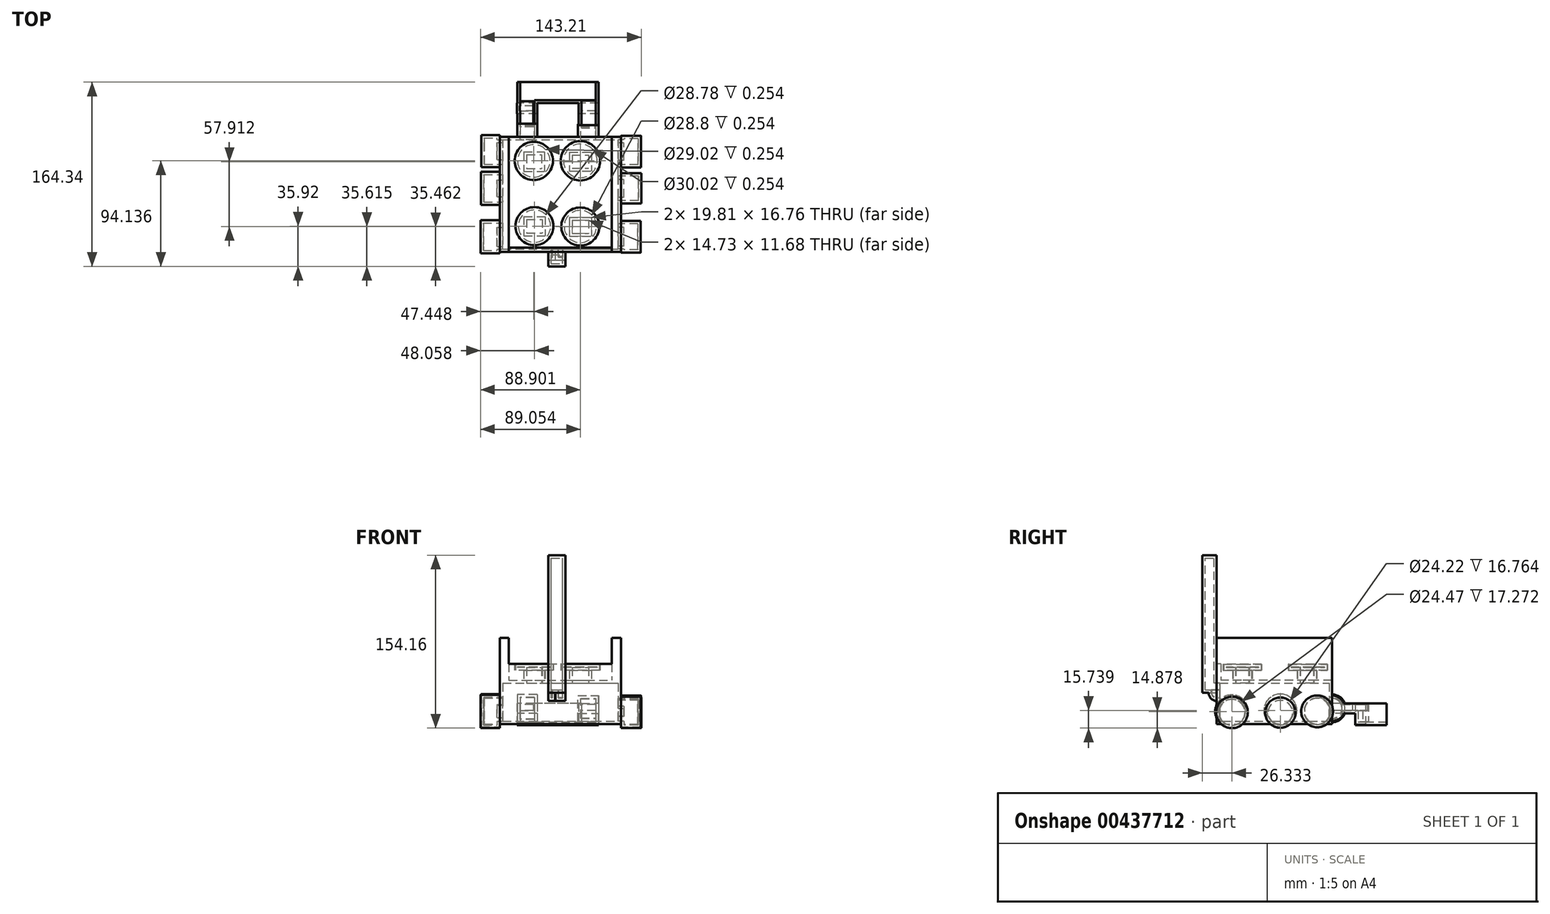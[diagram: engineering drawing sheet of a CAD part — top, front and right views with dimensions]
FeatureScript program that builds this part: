
annotation { "Feature Type Name" : "Feature", "Feature Type Description" : "" }
export const myFeature = defineFeature(function(context is Context, id is Id, definition is map)
    precondition{}
    {
        {
            var Q0;
            Q0=qCreatedBy(makeId("Front.planeOp"),FACE);
            var sketch = newSketch(context, id + "F0", { "sketchPlane" : qUnion([Q0])});
            skLineSegment(sketch, "E0.bottom", {"start": v(-50.6, 20.57) * mm, "end": v(57.3, 20.57) * mm});
            skLineSegment(sketch, "E0.top", {"start": v(-50.6, -18.44) * mm, "end": v(57.3, -18.44) * mm});
            skLineSegment(sketch, "E0.left", {"start": v(-50.6, 20.57) * mm, "end": v(-50.6, -18.44) * mm});
            skLineSegment(sketch, "E0.right", {"start": v(57.3, 20.57) * mm, "end": v(57.3, -18.44) * mm});
            skSolve(sketch);
        }
        {
            var Q0;
            Q0 = qSketchRegion(id + "F0", true);
            extrude(context, id + "F1", {"entities" : qUnion([Q0]), "depth" : 56.64 * mm});
        }
        {
            var Q0;
            Q0=makeQuery(id+"F1.opExtrude","CAP_FACE",FACE,{"disambiguationData":[OSD([sQuery(id+"F0.wireOp",EDGE,"E0.bottom"),sQuery(id+"F0.wireOp",EDGE,"E0.top"),sQuery(id+"F0.wireOp",EDGE,"E0.left"),sQuery(id+"F0.wireOp",EDGE,"E0.right")])],"isStart":true});
            extrude(context, id + "F2", {"entities" : qUnion([Q0]), "operationType" : NewBodyOperationType.ADD, "depth" : 45.97 * mm});
        }
        {
            var Q0;
            {var subQ0=sQuery(id+"F0.wireOp",EDGE,"E0.right");Q0=makeQuery(id+"F2.boolean.opBoolean","MERGE",FACE,{"derivedFrom":[makeQuery(id+"F1.opExtrude","SWEPT_FACE",FACE,{"disambiguationData":[OSD([subQ0])]}),makeQuery(id+"F2.opExtrude","SWEPT_FACE",FACE,{"disambiguationData":[OSD([subQ0])]})]});}
            var sketch = newSketch(context, id + "F3", { "sketchPlane" : qUnion([Q0])});
            skCircle(sketch, "E1", {"center": v(-43.07, -8.03) * mm, "radius": 14.07 * mm});
            skSolve(sketch);
        }
        {
            var Q0;
            Q0 = qSketchRegion(id + "F3", true);
            extrude(context, id + "F4", {"entities" : qUnion([Q0]), "operationType" : NewBodyOperationType.ADD, "depth" : 17.53 * mm});
        }
        {
            var Q0;
            {var subQ0=sQuery(id+"F0.wireOp",EDGE,"E0.bottom");var subQ1=sQuery(id+"F0.wireOp",EDGE,"E0.top");var subQ2=sQuery(id+"F0.wireOp",EDGE,"E0.right");var subQ3=sQuery(id+"F0.wireOp",EDGE,"E0.left");var subQ4=sQuery(id+"F3.wireOp",EDGE,"E1");Q0=makeQuery(id+"F4.boolean.opBoolean","SPLIT",FACE,{"disambiguationData":[TD([makeQuery(id+"F1.opExtrude","SWEPT_FACE",FACE,{"disambiguationData":[OSD([subQ0])]}),makeQuery(id+"F1.opExtrude","CAP_FACE",FACE,{"disambiguationData":[OSD([subQ0,subQ1,subQ3,subQ2])],"isStart":false}),makeQuery(id+"F1.opExtrude","SWEPT_FACE",FACE,{"disambiguationData":[OSD([subQ1])]}),makeQuery(id+"F2.opExtrude","SWEPT_FACE",FACE,{"disambiguationData":[OSD([subQ0])]}),makeQuery(id+"F2.opExtrude","SWEPT_FACE",FACE,{"disambiguationData":[OSD([subQ1])]}),makeQuery(id+"F2.opExtrude","CAP_FACE",FACE,{"disambiguationData":[OSD([subQ0,subQ1,subQ3,subQ2])],"isStart":false}),makeQuery(id+"F4.opExtrude","SWEPT_FACE",FACE,{"disambiguationData":[OSD([subQ4])]}),makeQuery(id+"F4.opExtrude","CAP_FACE",FACE,{"disambiguationData":[OSD([subQ4])],"isStart":true})])],"derivedFrom":makeQuery(id+"F2.boolean.opBoolean","MERGE",FACE,{"derivedFrom":[makeQuery(id+"F1.opExtrude","SWEPT_FACE",FACE,{"disambiguationData":[OSD([subQ2])]}),makeQuery(id+"F2.opExtrude","SWEPT_FACE",FACE,{"disambiguationData":[OSD([subQ2])]})]})});}
            var sketch = newSketch(context, id + "F5", { "sketchPlane" : qUnion([Q0])});
            skCircle(sketch, "E2", {"center": v(0, -8.32) * mm, "radius": 13.5 * mm});
            skSolve(sketch);
        }
        {
            var Q0;
            Q0 = qSketchRegion(id + "F5", true);
            extrude(context, id + "F6", {"entities" : qUnion([Q0]), "operationType" : NewBodyOperationType.ADD, "depth" : 18.03 * mm});
        }
        {
            var Q0;
            {var subQ0=sQuery(id+"F0.wireOp",EDGE,"E0.bottom");var subQ1=sQuery(id+"F0.wireOp",EDGE,"E0.top");var subQ2=sQuery(id+"F0.wireOp",EDGE,"E0.right");var subQ3=sQuery(id+"F0.wireOp",EDGE,"E0.left");var subQ4=sQuery(id+"F3.wireOp",EDGE,"E1");Q0=makeQuery(id+"F4.boolean.opBoolean","SPLIT",FACE,{"disambiguationData":[TD([makeQuery(id+"F1.opExtrude","SWEPT_FACE",FACE,{"disambiguationData":[OSD([subQ0])]}),makeQuery(id+"F1.opExtrude","CAP_FACE",FACE,{"disambiguationData":[OSD([subQ0,subQ1,subQ3,subQ2])],"isStart":false}),makeQuery(id+"F1.opExtrude","SWEPT_FACE",FACE,{"disambiguationData":[OSD([subQ1])]}),makeQuery(id+"F2.opExtrude","SWEPT_FACE",FACE,{"disambiguationData":[OSD([subQ0])]}),makeQuery(id+"F2.opExtrude","SWEPT_FACE",FACE,{"disambiguationData":[OSD([subQ1])]}),makeQuery(id+"F2.opExtrude","CAP_FACE",FACE,{"disambiguationData":[OSD([subQ0,subQ1,subQ3,subQ2])],"isStart":false}),makeQuery(id+"F4.opExtrude","SWEPT_FACE",FACE,{"disambiguationData":[OSD([subQ4])]}),makeQuery(id+"F4.opExtrude","CAP_FACE",FACE,{"disambiguationData":[OSD([subQ4])],"isStart":true})])],"derivedFrom":makeQuery(id+"F2.boolean.opBoolean","MERGE",FACE,{"derivedFrom":[makeQuery(id+"F1.opExtrude","SWEPT_FACE",FACE,{"disambiguationData":[OSD([subQ2])]}),makeQuery(id+"F2.opExtrude","SWEPT_FACE",FACE,{"disambiguationData":[OSD([subQ2])]})]})});}
            var sketch = newSketch(context, id + "F7", { "sketchPlane" : qUnion([Q0])});
            skCircle(sketch, "E3", {"center": v(32.74, -7.15) * mm, "radius": 14.18 * mm});
            skSolve(sketch);
        }
        {
            var Q0;
            Q0 = qSketchRegion(id + "F7", true);
            extrude(context, id + "F8", {"entities" : qUnion([Q0]), "operationType" : NewBodyOperationType.ADD, "depth" : 17.78 * mm});
        }
        {
            var Q0;
            {var subQ0=sQuery(id+"F0.wireOp",EDGE,"E0.left");Q0=makeQuery(id+"F2.boolean.opBoolean","MERGE",FACE,{"derivedFrom":[makeQuery(id+"F1.opExtrude","SWEPT_FACE",FACE,{"disambiguationData":[OSD([subQ0])]}),makeQuery(id+"F2.opExtrude","SWEPT_FACE",FACE,{"disambiguationData":[OSD([subQ0])]})]});}
            var sketch = newSketch(context, id + "F9", { "sketchPlane" : qUnion([Q0])});
            skCircle(sketch, "E4", {"center": v(-33.23, -6.92) * mm, "radius": 14.3 * mm});
            skSolve(sketch);
        }
        {
            var Q0;
            Q0 = qSketchRegion(id + "F9", true);
            extrude(context, id + "F10", {"entities" : qUnion([Q0]), "operationType" : NewBodyOperationType.ADD, "depth" : 16.5 * mm});
        }
        {
            var Q0;
            {var subQ0=sQuery(id+"F0.wireOp",EDGE,"E0.bottom");var subQ1=sQuery(id+"F9.wireOp",EDGE,"E4");var subQ2=sQuery(id+"F0.wireOp",EDGE,"E0.top");var subQ3=sQuery(id+"F0.wireOp",EDGE,"E0.right");var subQ4=sQuery(id+"F0.wireOp",EDGE,"E0.left");Q0=makeQuery(id+"F10.boolean.opBoolean","SPLIT",FACE,{"disambiguationData":[TD([makeQuery(id+"F1.opExtrude","SWEPT_FACE",FACE,{"disambiguationData":[OSD([subQ0])]}),makeQuery(id+"F1.opExtrude","CAP_FACE",FACE,{"disambiguationData":[OSD([subQ0,subQ2,subQ4,subQ3])],"isStart":false}),makeQuery(id+"F1.opExtrude","SWEPT_FACE",FACE,{"disambiguationData":[OSD([subQ2])]}),makeQuery(id+"F2.opExtrude","SWEPT_FACE",FACE,{"disambiguationData":[OSD([subQ0])]}),makeQuery(id+"F2.opExtrude","SWEPT_FACE",FACE,{"disambiguationData":[OSD([subQ2])]}),makeQuery(id+"F2.opExtrude","CAP_FACE",FACE,{"disambiguationData":[OSD([subQ0,subQ2,subQ4,subQ3])],"isStart":false}),makeQuery(id+"F10.opExtrude","SWEPT_FACE",FACE,{"disambiguationData":[OSD([subQ1])]}),makeQuery(id+"F10.opExtrude","CAP_FACE",FACE,{"disambiguationData":[OSD([subQ1])],"isStart":true})])],"derivedFrom":makeQuery(id+"F2.boolean.opBoolean","MERGE",FACE,{"derivedFrom":[makeQuery(id+"F1.opExtrude","SWEPT_FACE",FACE,{"disambiguationData":[OSD([subQ4])]}),makeQuery(id+"F2.opExtrude","SWEPT_FACE",FACE,{"disambiguationData":[OSD([subQ4])]})]})});}
            var sketch = newSketch(context, id + "F11", { "sketchPlane" : qUnion([Q0])});
            skCircle(sketch, "E5", {"center": v(0, -6.35) * mm, "radius": 14.65 * mm});
            skSolve(sketch);
        }
        {
            var Q0;
            Q0 = qSketchRegion(id + "F11", true);
            extrude(context, id + "F12", {"entities" : qUnion([Q0]), "operationType" : NewBodyOperationType.ADD, "depth" : 16.76 * mm});
        }
        {
            var Q0;
            {var subQ0=sQuery(id+"F0.wireOp",EDGE,"E0.bottom");var subQ1=sQuery(id+"F9.wireOp",EDGE,"E4");var subQ2=sQuery(id+"F0.wireOp",EDGE,"E0.top");var subQ3=sQuery(id+"F0.wireOp",EDGE,"E0.right");var subQ4=sQuery(id+"F0.wireOp",EDGE,"E0.left");Q0=makeQuery(id+"F10.boolean.opBoolean","SPLIT",FACE,{"disambiguationData":[TD([makeQuery(id+"F1.opExtrude","SWEPT_FACE",FACE,{"disambiguationData":[OSD([subQ0])]}),makeQuery(id+"F1.opExtrude","CAP_FACE",FACE,{"disambiguationData":[OSD([subQ0,subQ2,subQ4,subQ3])],"isStart":false}),makeQuery(id+"F1.opExtrude","SWEPT_FACE",FACE,{"disambiguationData":[OSD([subQ2])]}),makeQuery(id+"F2.opExtrude","SWEPT_FACE",FACE,{"disambiguationData":[OSD([subQ0])]}),makeQuery(id+"F2.opExtrude","SWEPT_FACE",FACE,{"disambiguationData":[OSD([subQ2])]}),makeQuery(id+"F2.opExtrude","CAP_FACE",FACE,{"disambiguationData":[OSD([subQ0,subQ2,subQ4,subQ3])],"isStart":false}),makeQuery(id+"F10.opExtrude","SWEPT_FACE",FACE,{"disambiguationData":[OSD([subQ1])]}),makeQuery(id+"F10.opExtrude","CAP_FACE",FACE,{"disambiguationData":[OSD([subQ1])],"isStart":true})])],"derivedFrom":makeQuery(id+"F2.boolean.opBoolean","MERGE",FACE,{"derivedFrom":[makeQuery(id+"F1.opExtrude","SWEPT_FACE",FACE,{"disambiguationData":[OSD([subQ4])]}),makeQuery(id+"F2.opExtrude","SWEPT_FACE",FACE,{"disambiguationData":[OSD([subQ4])]})]})});}
            var sketch = newSketch(context, id + "F13", { "sketchPlane" : qUnion([Q0])});
            skCircle(sketch, "E6", {"center": v(43.27, -7.21) * mm, "radius": 14.77 * mm});
            skSolve(sketch);
        }
        {
            var Q0;
            Q0 = qSketchRegion(id + "F13", true);
            extrude(context, id + "F14", {"entities" : qUnion([Q0]), "operationType" : NewBodyOperationType.ADD, "depth" : 17.27 * mm});
        }
        {
            var Q0;
            Q0=makeQuery(id+"F2.opExtrude","CAP_FACE",FACE,{"disambiguationData":[OSD([sQuery(id+"F0.wireOp",EDGE,"E0.bottom"),sQuery(id+"F0.wireOp",EDGE,"E0.top"),sQuery(id+"F0.wireOp",EDGE,"E0.left"),sQuery(id+"F0.wireOp",EDGE,"E0.right")])],"isStart":false});
            var sketch = newSketch(context, id + "F15", { "sketchPlane" : qUnion([Q0])});
            skLineSegment(sketch, "E7.bottom", {"start": v(-37.25, 0) * mm, "end": v(-19.46, 0) * mm});
            skLineSegment(sketch, "E7.top", {"start": v(-37.25, -8.93) * mm, "end": v(-19.46, -8.93) * mm});
            skLineSegment(sketch, "E7.left", {"start": v(-37.25, 0) * mm, "end": v(-37.25, -8.93) * mm});
            skLineSegment(sketch, "E7.right", {"start": v(-19.46, 0) * mm, "end": v(-19.46, -8.93) * mm});
            skLineSegment(sketch, "E8.bottom", {"start": v(17.28, 0) * mm, "end": v(35.07, 0) * mm});
            skLineSegment(sketch, "E8.top", {"start": v(17.28, -8.93) * mm, "end": v(35.07, -8.93) * mm});
            skLineSegment(sketch, "E8.left", {"start": v(17.28, 0) * mm, "end": v(17.28, -8.93) * mm});
            skLineSegment(sketch, "E8.right", {"start": v(35.07, 0) * mm, "end": v(35.07, -8.93) * mm});
            skSolve(sketch);
        }
        {
            var Q0;
            Q0 = qSketchRegion(id + "F15", true);
            extrude(context, id + "F16", {"entities" : qUnion([Q0]), "operationType" : NewBodyOperationType.ADD, "depth" : 20.57 * mm});
        }
        {
            var Q0;
            Q0=makeQuery(id+"F16.opExtrude","CAP_FACE",FACE,{"disambiguationData":[OSD([sQuery(id+"F15.wireOp",EDGE,"E7.bottom"),sQuery(id+"F15.wireOp",EDGE,"E7.top"),sQuery(id+"F15.wireOp",EDGE,"E7.left"),sQuery(id+"F15.wireOp",EDGE,"E7.right")])],"isStart":false});
            var sketch = newSketch(context, id + "F17", { "sketchPlane" : qUnion([Q0])});
            skLineSegment(sketch, "E9.bottom", {"start": v(-37.25, 0) * mm, "end": v(-19.46, 0) * mm});
            skLineSegment(sketch, "E9.top", {"start": v(-37.25, -19.27) * mm, "end": v(-19.46, -19.27) * mm});
            skLineSegment(sketch, "E9.left", {"start": v(-37.25, 0) * mm, "end": v(-37.25, -19.27) * mm});
            skLineSegment(sketch, "E9.right", {"start": v(-19.46, 0) * mm, "end": v(-19.46, -19.27) * mm});
            skLineSegment(sketch, "E10.bottom", {"start": v(17.47, 0) * mm, "end": v(35.27, 0) * mm});
            skLineSegment(sketch, "E10.top", {"start": v(17.47, -19.55) * mm, "end": v(35.27, -19.55) * mm});
            skLineSegment(sketch, "E10.left", {"start": v(17.47, 0) * mm, "end": v(17.47, -19.55) * mm});
            skLineSegment(sketch, "E10.right", {"start": v(35.27, 0) * mm, "end": v(35.27, -19.55) * mm});
            skSolve(sketch);
        }
        {
            var Q0;
            Q0 = qSketchRegion(id + "F17", true);
            extrude(context, id + "F18", {"entities" : qUnion([Q0]), "operationType" : NewBodyOperationType.ADD, "depth" : 9.4 * mm});
        }
        {
            var Q0;
            Q0=makeQuery(id+"F1.opExtrude","CAP_FACE",FACE,{"disambiguationData":[OSD([sQuery(id+"F0.wireOp",EDGE,"E0.bottom"),sQuery(id+"F0.wireOp",EDGE,"E0.top"),sQuery(id+"F0.wireOp",EDGE,"E0.left"),sQuery(id+"F0.wireOp",EDGE,"E0.right")])],"isStart":false});
            var sketch = newSketch(context, id + "F19", { "sketchPlane" : qUnion([Q0])});
            skLineSegment(sketch, "E11.bottom", {"start": v(-7.4, 9.33) * mm, "end": v(7.74, 9.33) * mm});
            skLineSegment(sketch, "E11.top", {"start": v(-7.4, 132.07) * mm, "end": v(7.74, 132.07) * mm});
            skLineSegment(sketch, "E11.left", {"start": v(-7.4, 9.33) * mm, "end": v(-7.4, 132.07) * mm});
            skLineSegment(sketch, "E11.right", {"start": v(7.74, 9.33) * mm, "end": v(7.74, 132.07) * mm});
            skSolve(sketch);
        }
        {
            var Q0;
            Q0 = qSketchRegion(id + "F19", true);
            extrude(context, id + "F20", {"entities" : qUnion([Q0]), "operationType" : NewBodyOperationType.ADD, "depth" : 12.95 * mm});
        }
        {
            var Q0;
            Q0=makeQuery(id+"F20.opExtrude","SWEPT_FACE",FACE,{"disambiguationData":[OSD([sQuery(id+"F19.wireOp",EDGE,"E11.left")])]});
            var sketch = newSketch(context, id + "F21", { "sketchPlane" : qUnion([Q0])});
            skCircle(sketch, "E12", {"center": v(55.15, 11.38) * mm, "radius": 9.31 * mm});
            skPoint(sketch, "E12.first.point", {"position": v(63.75, 14.95) * mm});
            skPoint(sketch, "E12.first.point.positionSnap0", {"position": v(56.64, 14.95) * mm});
            skPoint(sketch, "E12.second.point", {"position": v(46.93, 7) * mm});
            skPoint(sketch, "E12.third.point", {"position": v(56.64, 20.57) * mm});
            skSolve(sketch);
        }
        {
            var Q0;
            Q0 = qSketchRegion(id + "F21", true);
            extrude(context, id + "F22", {"entities" : qUnion([Q0]), "operationType" : NewBodyOperationType.ADD, "oppositeDirection" : true, "depth" : 6.1 * mm});
        }
        {
            var Q0;
            Q0=makeQuery(id+"F20.opExtrude","SWEPT_FACE",FACE,{"disambiguationData":[OSD([sQuery(id+"F19.wireOp",EDGE,"E11.right")])]});
            var sketch = newSketch(context, id + "F23", { "sketchPlane" : qUnion([Q0])});
            skCircle(sketch, "E13", {"center": v(-56.64, 9.33) * mm, "radius": 7.21 * mm});
            skSolve(sketch);
        }
        {
            var Q0;
            Q0 = qSketchRegion(id + "F23", true);
            extrude(context, id + "F24", {"entities" : qUnion([Q0]), "operationType" : NewBodyOperationType.ADD, "oppositeDirection" : true, "depth" : 8.9 * mm});
        }
        {
            var Q0;
            {var subQ0=sQuery(id+"F0.wireOp",EDGE,"E0.bottom");Q0=makeQuery(id+"F2.boolean.opBoolean","MERGE",FACE,{"derivedFrom":[makeQuery(id+"F1.opExtrude","SWEPT_FACE",FACE,{"disambiguationData":[OSD([subQ0])]}),makeQuery(id+"F2.opExtrude","SWEPT_FACE",FACE,{"disambiguationData":[OSD([subQ0])]})]});}
            var sketch = newSketch(context, id + "F25", { "sketchPlane" : qUnion([Q0])});
            skLineSegment(sketch, "E14.bottom", {"start": v(-29.26, -25.15) * mm, "end": v(-10.36, -25.15) * mm});
            skLineSegment(sketch, "E14.top", {"start": v(-29.26, -42.21) * mm, "end": v(-10.36, -42.21) * mm});
            skLineSegment(sketch, "E14.left", {"start": v(-29.26, -25.15) * mm, "end": v(-29.26, -42.21) * mm});
            skLineSegment(sketch, "E14.right", {"start": v(-10.36, -25.15) * mm, "end": v(-10.36, -42.21) * mm});
            skLineSegment(sketch, "E15.bottom", {"start": v(11.28, -25.76) * mm, "end": v(31.09, -25.76) * mm});
            skLineSegment(sketch, "E15.top", {"start": v(11.28, -42.52) * mm, "end": v(31.09, -42.52) * mm});
            skLineSegment(sketch, "E15.left", {"start": v(11.28, -25.76) * mm, "end": v(11.28, -42.52) * mm});
            skLineSegment(sketch, "E15.right", {"start": v(31.09, -25.76) * mm, "end": v(31.09, -42.52) * mm});
            skLineSegment(sketch, "E16.bottom", {"start": v(-29.26, 32.46) * mm, "end": v(-10.97, 32.46) * mm});
            skLineSegment(sketch, "E16.top", {"start": v(-29.26, 15.09) * mm, "end": v(-10.97, 15.09) * mm});
            skLineSegment(sketch, "E16.left", {"start": v(-29.26, 32.46) * mm, "end": v(-29.26, 15.09) * mm});
            skLineSegment(sketch, "E16.right", {"start": v(-10.97, 32.46) * mm, "end": v(-10.97, 15.09) * mm});
            skLineSegment(sketch, "E17.bottom", {"start": v(11.28, 32.16) * mm, "end": v(31.09, 32.16) * mm});
            skLineSegment(sketch, "E17.top", {"start": v(11.28, 15.4) * mm, "end": v(31.09, 15.4) * mm});
            skLineSegment(sketch, "E17.left", {"start": v(11.28, 32.16) * mm, "end": v(11.28, 15.4) * mm});
            skLineSegment(sketch, "E17.right", {"start": v(31.09, 32.16) * mm, "end": v(31.09, 15.4) * mm});
            skSolve(sketch);
        }
        {
            var Q0;
            Q0 = qSketchRegion(id + "F25", true);
            extrude(context, id + "F26", {"entities" : qUnion([Q0]), "operationType" : NewBodyOperationType.ADD, "depth" : 8.9 * mm});
        }
        {
            var Q0;
            Q0=makeQuery(id+"F26.opExtrude","CAP_FACE",FACE,{"disambiguationData":[OSD([sQuery(id+"F25.wireOp",EDGE,"E14.bottom"),sQuery(id+"F25.wireOp",EDGE,"E14.top"),sQuery(id+"F25.wireOp",EDGE,"E14.left"),sQuery(id+"F25.wireOp",EDGE,"E14.right")])],"isStart":false});
            var sketch = newSketch(context, id + "F27", { "sketchPlane" : qUnion([Q0])});
            skCircle(sketch, "E18", {"center": v(-19.81, -33.68) * mm, "radius": 16.93 * mm});
            skCircle(sketch, "E19", {"center": v(21.03, -33.99) * mm, "radius": 16.94 * mm});
            skCircle(sketch, "E20", {"center": v(-20.42, 24.54) * mm, "radius": 17.05 * mm});
            skCircle(sketch, "E21", {"center": v(21.03, 24.54) * mm, "radius": 17.55 * mm});
            skSolve(sketch);
        }
        {
            var Q0;
            Q0 = qSketchRegion(id + "F27", true);
            extrude(context, id + "F28", {"entities" : qUnion([Q0]), "operationType" : NewBodyOperationType.ADD, "depth" : 5.33 * mm});
        }
        {
            var Q0;
            Q0=makeQuery(id+"F18.opExtrude","CAP_FACE",FACE,{"disambiguationData":[OSD([sQuery(id+"F17.wireOp",EDGE,"E9.bottom"),sQuery(id+"F17.wireOp",EDGE,"E9.top"),sQuery(id+"F17.wireOp",EDGE,"E9.left"),sQuery(id+"F17.wireOp",EDGE,"E9.right")])],"isStart":false});
            var sketch = newSketch(context, id + "F29", { "sketchPlane" : qUnion([Q0])});
            skLineSegment(sketch, "E22.bottom", {"start": v(-37.25, 0) * mm, "end": v(34.99, 0) * mm});
            skLineSegment(sketch, "E22.top", {"start": v(-37.25, -19.33) * mm, "end": v(34.99, -19.33) * mm});
            skLineSegment(sketch, "E22.left", {"start": v(-37.25, 0) * mm, "end": v(-37.25, -19.33) * mm});
            skLineSegment(sketch, "E22.right", {"start": v(34.99, 0) * mm, "end": v(34.99, -19.33) * mm});
            skSolve(sketch);
        }
        {
            var Q0;
            Q0 = qSketchRegion(id + "F29", true);
            extrude(context, id + "F30", {"entities" : qUnion([Q0]), "operationType" : NewBodyOperationType.ADD, "depth" : 18.8 * mm});
        }
        {
            var Q0;
            Q0=makeQuery(id+"F30.boolean.opBoolean","MERGE",FACE,{"derivedFrom":[makeQuery(id+"F18.boolean.opBoolean","MERGE",FACE,{"derivedFrom":[makeQuery(id+"F16.opExtrude","SWEPT_FACE",FACE,{"disambiguationData":[OSD([sQuery(id+"F15.wireOp",EDGE,"E7.left")])]}),makeQuery(id+"F18.opExtrude","SWEPT_FACE",FACE,{"disambiguationData":[OSD([sQuery(id+"F17.wireOp",EDGE,"E9.left")])]})]}),makeQuery(id+"F30.opExtrude","SWEPT_FACE",FACE,{"disambiguationData":[OSD([sQuery(id+"F29.wireOp",EDGE,"E22.left")])]})]});
            var sketch = newSketch(context, id + "F31", { "sketchPlane" : qUnion([Q0])});
            skCircle(sketch, "E23", {"center": v(45.97, -4.47) * mm, "radius": 11.47 * mm});
            skSolve(sketch);
        }
        {
            var Q0;
            Q0=makeQuery(id+"F16.opExtrude","SWEPT_FACE",FACE,{"disambiguationData":[OSD([sQuery(id+"F15.wireOp",EDGE,"E8.right")])]});
            var sketch = newSketch(context, id + "F32", { "sketchPlane" : qUnion([Q0])});
            skCircle(sketch, "E24", {"center": v(-45.97, -4.47) * mm, "radius": 12.37 * mm});
            skSolve(sketch);
        }
        {
            var Q0;
            Q0 = qSketchRegion(id + "F32", true);
            extrude(context, id + "F33", {"entities" : qUnion([Q0]), "operationType" : NewBodyOperationType.ADD, "oppositeDirection" : true, "depth" : 17.78 * mm});
        }
        {
            var Q0;
            Q0 = qSketchRegion(id + "F31", true);
            extrude(context, id + "F34", {"entities" : qUnion([Q0]), "operationType" : NewBodyOperationType.ADD, "oppositeDirection" : true, "depth" : 18.29 * mm});
        }
        {
            var Q0;
            Q0=makeQuery(id+"F30.opExtrude","CAP_FACE",FACE,{"disambiguationData":[OSD([sQuery(id+"F29.wireOp",EDGE,"E22.bottom"),sQuery(id+"F29.wireOp",EDGE,"E22.top"),sQuery(id+"F29.wireOp",EDGE,"E22.left"),sQuery(id+"F29.wireOp",EDGE,"E22.right")])],"isStart":false});
            var Q1;
            Q1=makeQuery(id+"F30.boolean.opBoolean","MERGE",FACE,{"derivedFrom":[makeQuery(id+"F18.boolean.opBoolean","MERGE",FACE,{"derivedFrom":[makeQuery(id+"F16.opExtrude","SWEPT_FACE",FACE,{"disambiguationData":[OSD([sQuery(id+"F15.wireOp",EDGE,"E7.bottom")])]}),makeQuery(id+"F18.opExtrude","SWEPT_FACE",FACE,{"disambiguationData":[OSD([sQuery(id+"F17.wireOp",EDGE,"E9.bottom")])]})]}),makeQuery(id+"F18.boolean.opBoolean","MERGE",FACE,{"derivedFrom":[makeQuery(id+"F16.opExtrude","SWEPT_FACE",FACE,{"disambiguationData":[OSD([sQuery(id+"F15.wireOp",EDGE,"E8.bottom")])]}),makeQuery(id+"F18.opExtrude","SWEPT_FACE",FACE,{"disambiguationData":[OSD([sQuery(id+"F17.wireOp",EDGE,"E10.bottom")])]})]}),makeQuery(id+"F30.opExtrude","SWEPT_FACE",FACE,{"disambiguationData":[OSD([sQuery(id+"F29.wireOp",EDGE,"E22.bottom")])]})]});
            shell(context, id + "F35", {"entities" : qUnion([Q0, Q1]), "thickness" : 2.54 * mm});
        }
        {
            var Q0;
            Q0=makeQuery(id+"F35.opShell","OFFSET_FACE",FACE,{"disambiguationData":[OSD([sQuery(id+"F15.wireOp",EDGE,"E7.top")])]});
            var sketch = newSketch(context, id + "F36", { "sketchPlane" : qUnion([Q0])});
            skLineSegment(sketch, "E25.bottom", {"start": v(34.71, 54.7) * mm, "end": v(22, 54.7) * mm});
            skLineSegment(sketch, "E25.top", {"start": v(34.71, 78.2) * mm, "end": v(22, 78.2) * mm});
            skLineSegment(sketch, "E25.left", {"start": v(34.71, 54.7) * mm, "end": v(34.71, 78.2) * mm});
            skLineSegment(sketch, "E25.right", {"start": v(22, 54.7) * mm, "end": v(22, 78.2) * mm});
            skLineSegment(sketch, "E26.bottom", {"start": v(-20.83, 54.7) * mm, "end": v(-33.32, 54.7) * mm});
            skLineSegment(sketch, "E26.top", {"start": v(-20.83, 77.8) * mm, "end": v(-33.32, 77.8) * mm});
            skLineSegment(sketch, "E26.left", {"start": v(-20.83, 54.7) * mm, "end": v(-20.83, 77.8) * mm});
            skLineSegment(sketch, "E26.right", {"start": v(-33.32, 54.7) * mm, "end": v(-33.32, 77.8) * mm});
            skSolve(sketch);
        }
        {
            var Q0;
            Q0 = qSketchRegion(id + "F36", true);
            extrude(context, id + "F37", {"entities" : qUnion([Q0]), "operationType" : NewBodyOperationType.ADD, "depth" : 5.33 * mm});
        }
        {
            var Q0;
            {var subQ0=sQuery(id+"F0.wireOp",EDGE,"E0.bottom");Q0=makeQuery(id+"F2.boolean.opBoolean","MERGE",FACE,{"derivedFrom":[makeQuery(id+"F1.opExtrude","SWEPT_FACE",FACE,{"disambiguationData":[OSD([subQ0])]}),makeQuery(id+"F2.opExtrude","SWEPT_FACE",FACE,{"disambiguationData":[OSD([subQ0])]})]});}
            var sketch = newSketch(context, id + "F38", { "sketchPlane" : qUnion([Q0])});
            skLineSegment(sketch, "E27.bottom", {"start": v(-42.7, 45.97) * mm, "end": v(-50.6, 45.97) * mm});
            skLineSegment(sketch, "E27.top", {"start": v(-42.7, -56.64) * mm, "end": v(-50.6, -56.64) * mm});
            skLineSegment(sketch, "E27.left", {"start": v(-42.7, 45.97) * mm, "end": v(-42.7, -56.64) * mm});
            skLineSegment(sketch, "E27.right", {"start": v(-50.6, 45.97) * mm, "end": v(-50.6, -56.64) * mm});
            skLineSegment(sketch, "E28.bottom", {"start": v(57.3, 45.97) * mm, "end": v(49.18, 45.97) * mm});
            skLineSegment(sketch, "E28.top", {"start": v(57.3, -56.64) * mm, "end": v(49.18, -56.64) * mm});
            skLineSegment(sketch, "E28.left", {"start": v(57.3, 45.97) * mm, "end": v(57.3, -56.64) * mm});
            skLineSegment(sketch, "E28.right", {"start": v(49.18, 45.97) * mm, "end": v(49.18, -56.64) * mm});
            skSolve(sketch);
        }
        {
            var Q0;
            Q0 = qSketchRegion(id + "F38", true);
            extrude(context, id + "F39", {"entities" : qUnion([Q0]), "operationType" : NewBodyOperationType.ADD, "depth" : 37.85 * mm});
        }
        {
            var Q0;
            {var subQ0=sQuery(id+"F0.wireOp",EDGE,"E0.bottom");Q0=makeQuery(id+"F2.boolean.opBoolean","MERGE",FACE,{"derivedFrom":[makeQuery(id+"F1.opExtrude","SWEPT_FACE",FACE,{"disambiguationData":[OSD([subQ0])]}),makeQuery(id+"F2.opExtrude","SWEPT_FACE",FACE,{"disambiguationData":[OSD([subQ0])]})]});}
            var sketch = newSketch(context, id + "F40", { "sketchPlane" : qUnion([Q0])});
            skLineSegment(sketch, "E29.bottom", {"start": v(-42.7, -52.97) * mm, "end": v(49.18, -52.97) * mm});
            skLineSegment(sketch, "E29.top", {"start": v(-42.7, -56.64) * mm, "end": v(49.18, -56.64) * mm});
            skLineSegment(sketch, "E29.left", {"start": v(-42.7, -52.97) * mm, "end": v(-42.7, -56.64) * mm});
            skLineSegment(sketch, "E29.right", {"start": v(49.18, -52.97) * mm, "end": v(49.18, -56.64) * mm});
            skSolve(sketch);
        }
        {
            var Q0;
            Q0 = qSketchRegion(id + "F40", true);
            extrude(context, id + "F41", {"entities" : qUnion([Q0]), "operationType" : NewBodyOperationType.ADD, "depth" : 14.73 * mm});
        }
    });
